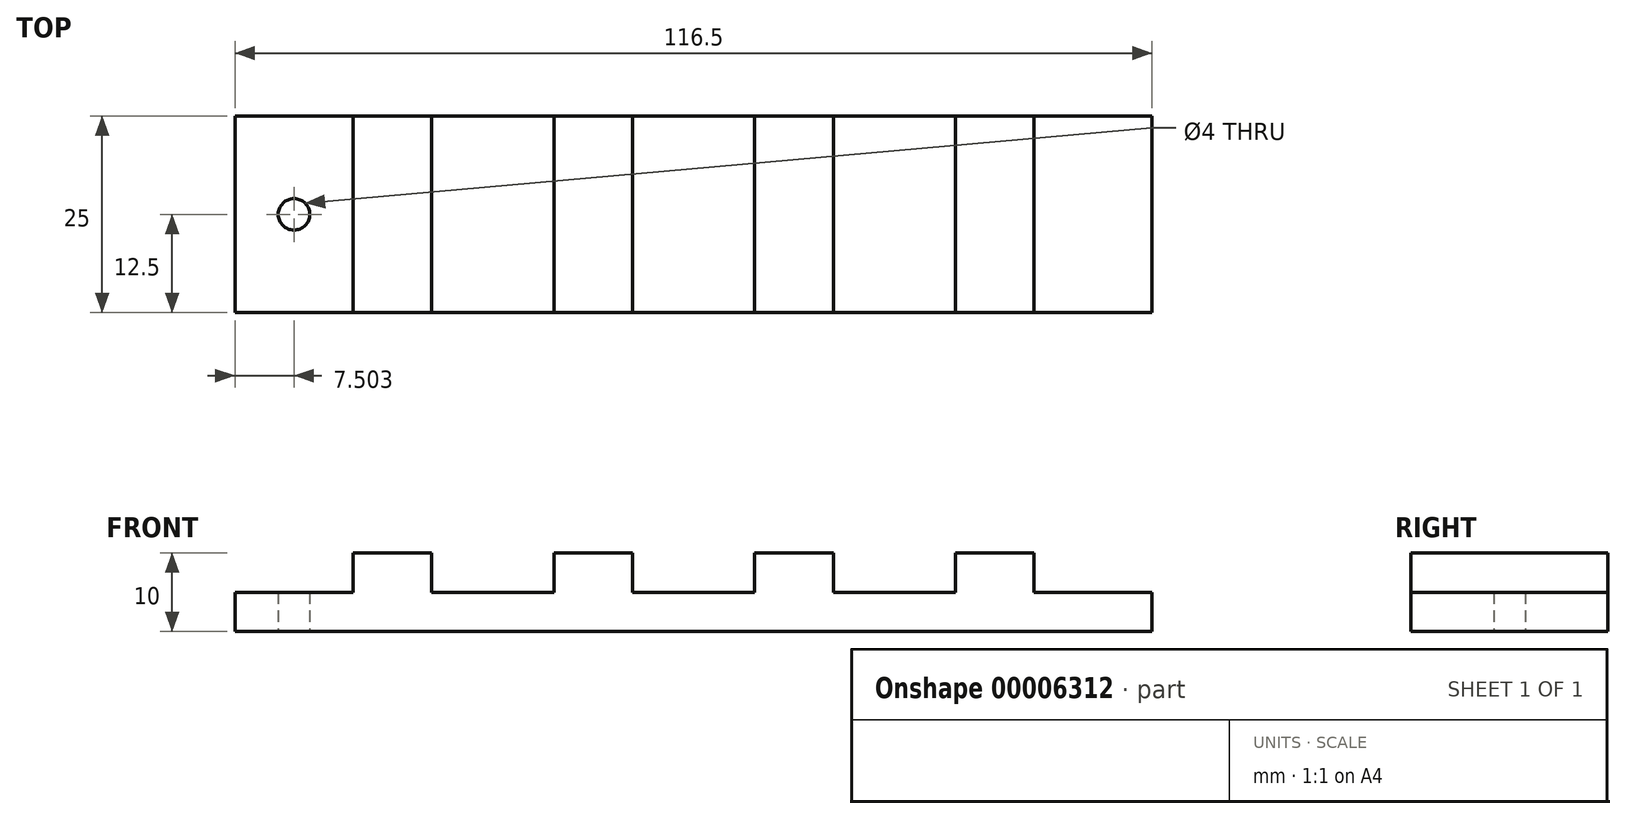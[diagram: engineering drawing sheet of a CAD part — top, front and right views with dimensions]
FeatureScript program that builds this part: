
annotation { "Feature Type Name" : "Feature", "Feature Type Description" : "" }
export const myFeature = defineFeature(function(context is Context, id is Id, definition is map)
    precondition{}
    {
        {
            var Q0;
            Q0=qCreatedBy(makeId("Front.planeOp"),FACE);
            var sketch = newSketch(context, id + "F0", { "sketchPlane" : qUnion([Q0])});
            skLineSegment(sketch, "E0", {"start": v(-175.86, 5) * mm, "end": v(-175.86, 10) * mm});
            skLineSegment(sketch, "E1", {"start": v(-175.86, 10) * mm, "end": v(-165.86, 10) * mm});
            skLineSegment(sketch, "E2", {"start": v(-165.86, 10) * mm, "end": v(-165.86, 5) * mm});
            skLineSegment(sketch, "E3", {"start": v(-165.86, 5) * mm, "end": v(-150.36, 5) * mm});
            skLineSegment(sketch, "E4", {"start": v(-150.36, 5) * mm, "end": v(-150.36, 10) * mm});
            skLineSegment(sketch, "E5", {"start": v(-150.36, 10) * mm, "end": v(-140.36, 10) * mm});
            skLineSegment(sketch, "E6", {"start": v(-140.36, 10) * mm, "end": v(-140.36, 5) * mm});
            skLineSegment(sketch, "E7", {"start": v(-140.36, 5) * mm, "end": v(-124.86, 5) * mm});
            skLineSegment(sketch, "E8", {"start": v(-124.86, 5) * mm, "end": v(-124.86, 10) * mm});
            skLineSegment(sketch, "E9", {"start": v(-124.86, 10) * mm, "end": v(-114.86, 10) * mm});
            skLineSegment(sketch, "E10", {"start": v(-114.86, 10) * mm, "end": v(-114.86, 5) * mm});
            skLineSegment(sketch, "E11", {"start": v(-114.86, 5) * mm, "end": v(-99.36, 5) * mm});
            skLineSegment(sketch, "E12", {"start": v(-99.36, 5) * mm, "end": v(-99.36, 10) * mm});
            skLineSegment(sketch, "E13", {"start": v(-99.36, 10) * mm, "end": v(-89.36, 10) * mm});
            skLineSegment(sketch, "E14", {"start": v(-89.36, 10) * mm, "end": v(-89.36, 5) * mm});
            skLineSegment(sketch, "E15", {"start": v(-74.36, 0) * mm, "end": v(-190.86, 0) * mm});
            skLineSegment(sketch, "E16.trimOffspring", {"start": v(-89.36, 5) * mm, "end": v(-74.36, 5) * mm});
            skLineSegment(sketch, "E17", {"start": v(-175.86, 5) * mm, "end": v(-190.86, 5) * mm});
            skLineSegment(sketch, "E18", {"start": v(-183.36, 5) * mm, "end": v(-183.36, -11.02) * mm, "construction": true});
            skLineSegment(sketch, "E19", {"start": v(-81.86, 5) * mm, "end": v(-81.86, -4.89) * mm, "construction": true});
            skLineSegment(sketch, "E20", {"start": v(-190.86, 5) * mm, "end": v(-190.86, 0) * mm});
            skLineSegment(sketch, "E21", {"start": v(-74.36, 5) * mm, "end": v(-74.36, 0) * mm});
            skSolve(sketch);
        }
        {
            var Q0;
            Q0=makeQuery(id+"F0.imprint","IMPRINT",FACE,{"disambiguationData":[TD([[makeQuery(id+"F0.imprint","IMPRINT",EDGE,{"derivedFrom":sQuery(id+"F0.wireOp",EDGE,"0b736146-ffee-45d5-a328-126a97785771")}),-1.0]])]});
            var Q1;
            Q1=makeQuery(id+"F0.imprint","IMPRINT",FACE,{"disambiguationData":[TD([[makeQuery(id+"F0.imprint","IMPRINT",EDGE,{"derivedFrom":sQuery(id+"F0.wireOp",EDGE,"E0")}),-1.0]])]});
            extrude(context, id + "F1", {"entities" : qUnion([Q0, Q1]), "depth" : 25 * mm});
        }
        {
            var Q0;
            Q0=qCreatedBy(makeId("Top.planeOp"),FACE);
            var sketch = newSketch(context, id + "F2", { "sketchPlane" : qUnion([Q0])});
            skCircle(sketch, "E22", {"center": v(-183.36, -12.5) * mm, "radius": 2 * mm});
            skLineSegment(sketch, "E23", {"start": v(-190.86, -12.5) * mm, "end": v(-74.36, -12.5) * mm, "construction": true});
            skLineSegment(sketch, "E24", {"start": v(-132.6, 20.47) * mm, "end": v(-132.6, -12.5) * mm, "construction": true});
            skCircle(sketch, "E25.1.MirrorC", {"center": v(-81.86, -12.5) * mm, "radius": 2 * mm});
            skSolve(sketch);
        }
        {
            var Q0;
            Q0=makeQuery(id+"F2.imprint","IMPRINT",FACE,{"disambiguationData":[TD([[makeQuery(id+"F2.imprint","IMPRINT",EDGE,{"derivedFrom":sQuery(id+"F2.wireOp",EDGE,"E22")}),1.0]])]});
            var Q1;
            Q1=makeQuery(id+"F2.imprint","IMPRINT",FACE,{"disambiguationData":[TD([[makeQuery(id+"F2.imprint","IMPRINT",EDGE,{"derivedFrom":sQuery(id+"F2.wireOp",EDGE,"E25.1.MirrorC")}),-1.0]])]});
            var Q2;
            Q2=sQuery(id+"F2.wireOp",EDGE,"E22");
            extrude(context, id + "F3", {"entities" : qUnion([Q0, Q1]), "operationType" : NewBodyOperationType.REMOVE, "surfaceEntities" : qUnion([Q2]), "endBound" : BoundingType.THROUGH_ALL, "depth" : 25 * mm});
        }
    });
